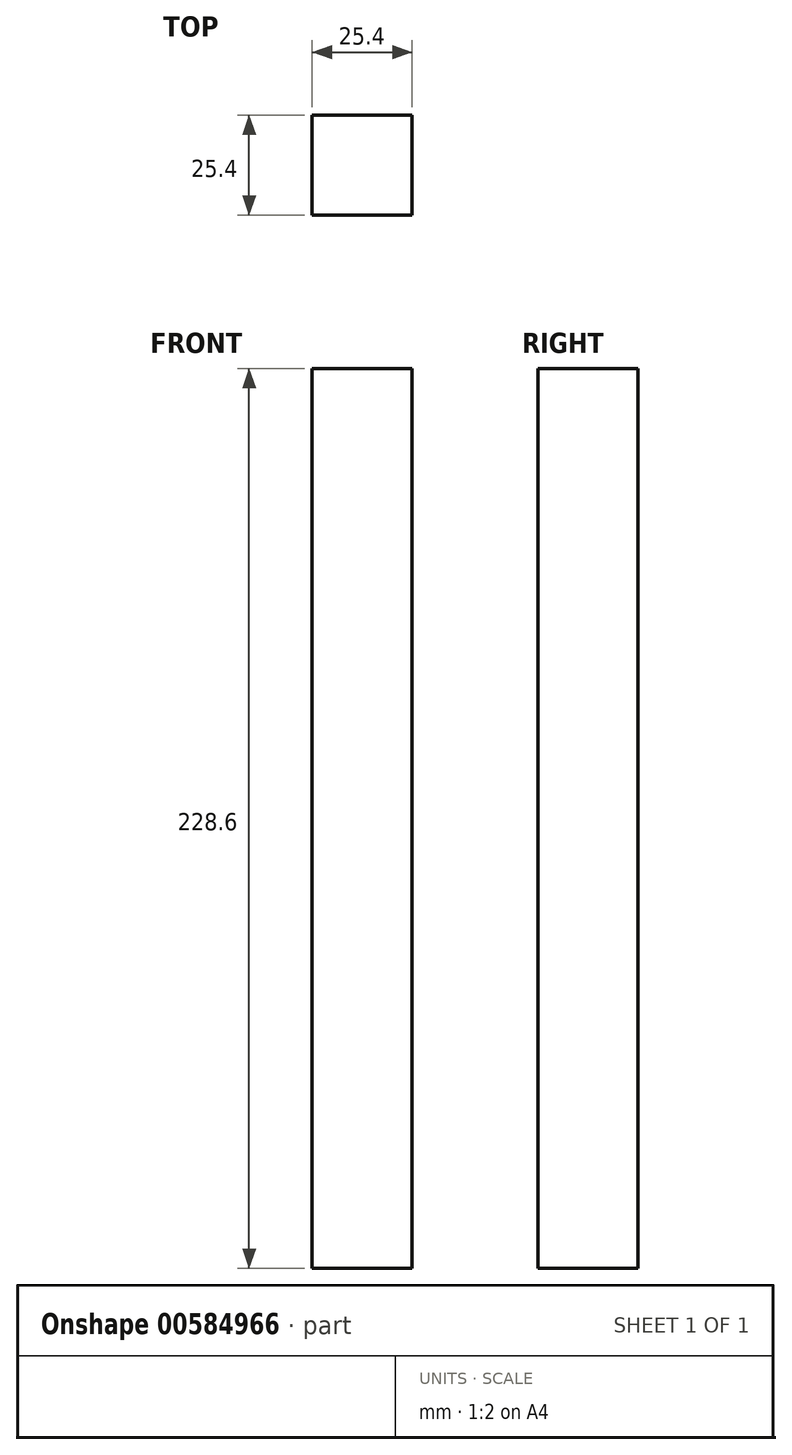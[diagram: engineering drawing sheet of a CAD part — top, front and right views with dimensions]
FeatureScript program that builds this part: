
annotation { "Feature Type Name" : "Feature", "Feature Type Description" : "" }
export const myFeature = defineFeature(function(context is Context, id is Id, definition is map)
    precondition{}
    {
        {
            var Q0;
            Q0=qCreatedBy(makeId("Top.planeOp"),FACE);
            var sketch = newSketch(context, id + "F0", { "sketchPlane" : qUnion([Q0])});
            skLineSegment(sketch, "E0.bottom", {"start": v(12.7, 12.7) * mm, "end": v(-12.7, 12.7) * mm});
            skLineSegment(sketch, "E0.top", {"start": v(12.7, -12.7) * mm, "end": v(-12.7, -12.7) * mm});
            skLineSegment(sketch, "E0.left", {"start": v(12.7, 12.7) * mm, "end": v(12.7, -12.7) * mm});
            skLineSegment(sketch, "E0.right", {"start": v(-12.7, 12.7) * mm, "end": v(-12.7, -12.7) * mm});
            skPoint(sketch, "E0.middle", {"position": v(0, 0) * mm});
            skSolve(sketch);
        }
        {
            var Q0;
            Q0=makeQuery(id+"F0.imprint","IMPRINT",FACE,{"disambiguationData":[TD([[makeQuery(id+"F0.imprint","IMPRINT",EDGE,{"derivedFrom":sQuery(id+"F0.wireOp",EDGE,"E0.bottom")}),1.0]])]});
            extrude(context, id + "F1", {"entities" : qUnion([Q0]), "depth" : 228.6 * mm, "offsetDistance" : 25.4 * mm});
        }
    });
